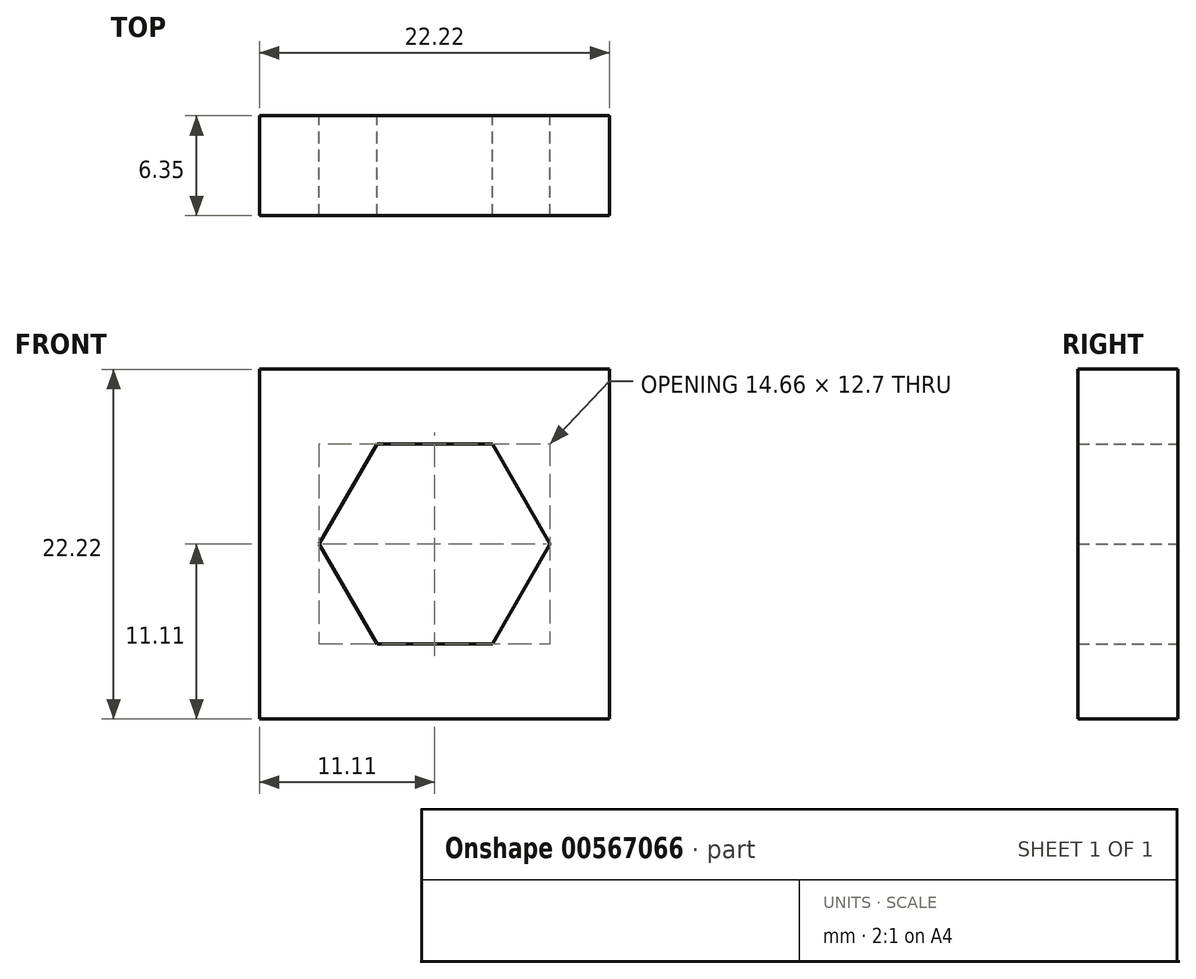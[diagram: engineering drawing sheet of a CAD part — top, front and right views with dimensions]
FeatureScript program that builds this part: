
annotation { "Feature Type Name" : "Feature", "Feature Type Description" : "" }
export const myFeature = defineFeature(function(context is Context, id is Id, definition is map)
    precondition{}
    {
        {
            var Q0;
            Q0=qCreatedBy(makeId("Front.planeOp"),FACE);
            var sketch = newSketch(context, id + "F0", { "sketchPlane" : qUnion([Q0])});
            skLineSegment(sketch, "E0.bottom", {"start": v(-11.11, 11.11) * mm, "end": v(11.11, 11.11) * mm});
            skLineSegment(sketch, "E0.top", {"start": v(-11.11, -11.11) * mm, "end": v(11.11, -11.11) * mm});
            skLineSegment(sketch, "E0.left", {"start": v(-11.11, 11.11) * mm, "end": v(-11.11, -11.11) * mm});
            skLineSegment(sketch, "E0.right", {"start": v(11.11, 11.11) * mm, "end": v(11.11, -11.11) * mm});
            skPoint(sketch, "E0.middle", {"position": v(0, 0) * mm});
            skCircle(sketch, "E1.cCircle", {"center": v(0, 0) * mm, "radius": 6.35 * mm, "construction": true});
            skLineSegment(sketch, "E1.0", {"start": v(-3.67, 6.35) * mm, "end": v(3.67, 6.35) * mm});
            skLineSegment(sketch, "E1.1", {"start": v(3.67, 6.35) * mm, "end": v(7.33, 0) * mm});
            skLineSegment(sketch, "E1.2", {"start": v(7.33, 0) * mm, "end": v(3.67, -6.35) * mm});
            skLineSegment(sketch, "E1.3", {"start": v(3.67, -6.35) * mm, "end": v(-3.67, -6.35) * mm});
            skLineSegment(sketch, "E1.4", {"start": v(-3.67, -6.35) * mm, "end": v(-7.33, 0) * mm});
            skLineSegment(sketch, "E1.5", {"start": v(-7.33, 0) * mm, "end": v(-3.67, 6.35) * mm});
            skPoint(sketch, "E1.0.midPoint", {"position": v(0, 6.35) * mm});
            skSolve(sketch);
        }
        {
            var Q0;
            Q0=qSketchRegion(id+"F0",true);
            extrude(context, id + "F1", {"entities" : qUnion([Q0]), "depth" : 6.35 * mm});
        }
    });
